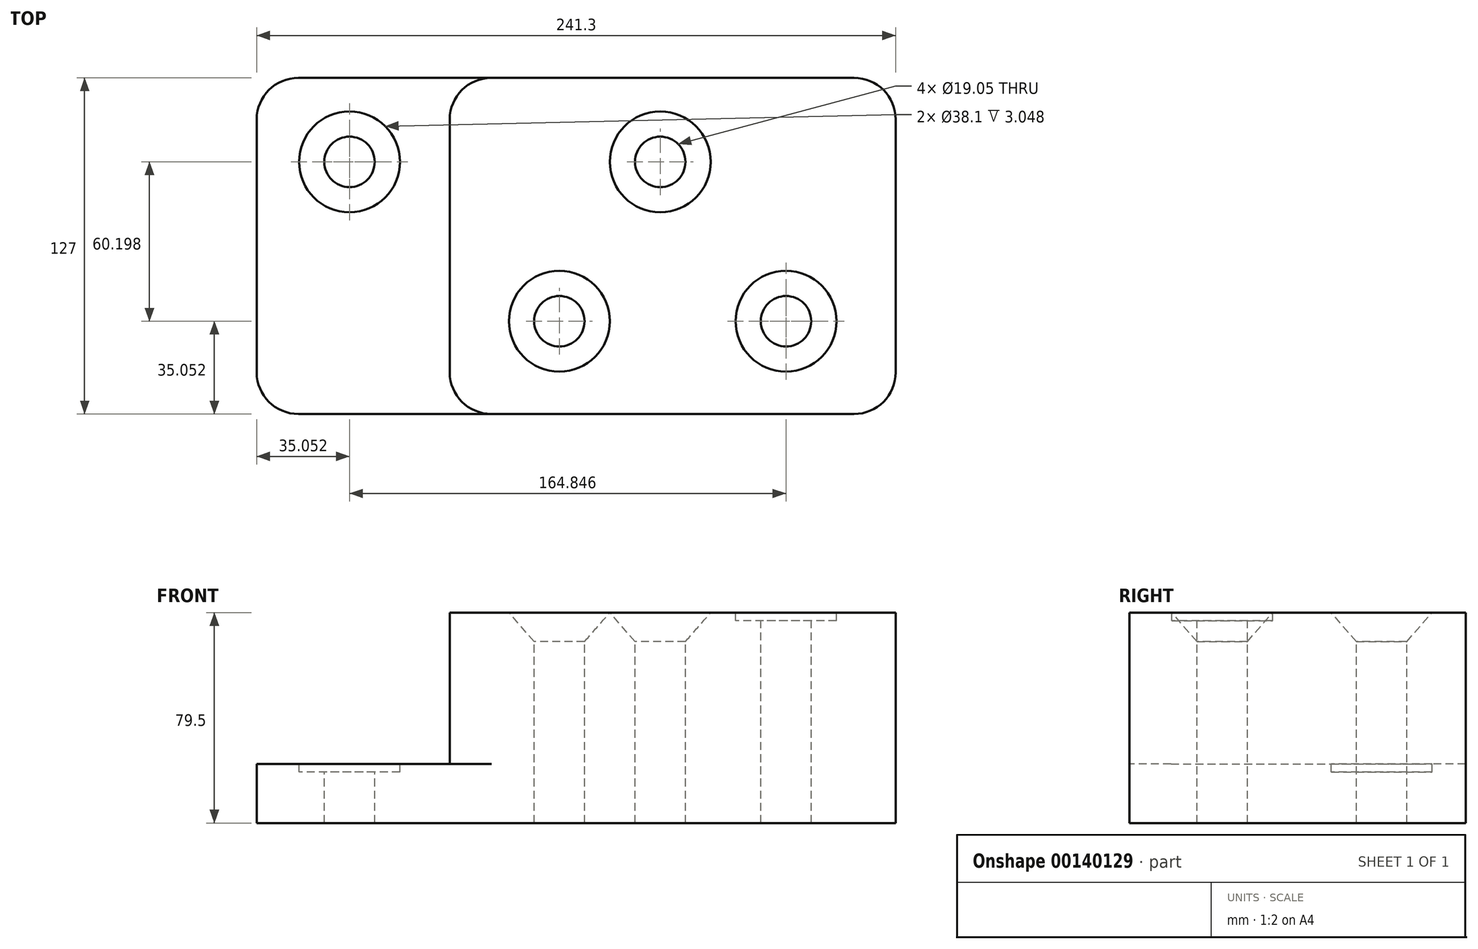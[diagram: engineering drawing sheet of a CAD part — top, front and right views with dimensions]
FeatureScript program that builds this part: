
annotation { "Feature Type Name" : "Feature", "Feature Type Description" : "" }
export const myFeature = defineFeature(function(context is Context, id is Id, definition is map)
    precondition{}
    {
        {
            var Q0;
            Q0=qCreatedBy(makeId("Top.planeOp"),FACE);
            var sketch = newSketch(context, id + "F0", { "sketchPlane" : qUnion([Q0])});
            skLineSegment(sketch, "E0.bottom", {"start": v(0, 0) * mm, "end": v(72.9, 0) * mm});
            skLineSegment(sketch, "E0.top", {"start": v(0, 127) * mm, "end": v(72.9, 127) * mm});
            skLineSegment(sketch, "E0.left", {"start": v(0, 0) * mm, "end": v(0, 127) * mm});
            skLineSegment(sketch, "E0.right", {"start": v(72.9, 0) * mm, "end": v(72.9, 127) * mm});
            skLineSegment(sketch, "E1.bottom", {"start": v(0, 0) * mm, "end": v(241.3, 0) * mm});
            skLineSegment(sketch, "E1.top", {"start": v(0, 127) * mm, "end": v(241.3, 127) * mm});
            skLineSegment(sketch, "E1.right", {"start": v(241.3, 0) * mm, "end": v(241.3, 127) * mm});
            skLineSegment(sketch, "E2", {"start": v(241.3, 127) * mm, "end": v(199.9, 127) * mm, "construction": true});
            skLineSegment(sketch, "E3", {"start": v(241.3, 127) * mm, "end": v(152.4, 127) * mm, "construction": true});
            skLineSegment(sketch, "E4", {"start": v(241.3, 127) * mm, "end": v(114.3, 127) * mm, "construction": true});
            skLineSegment(sketch, "E5", {"start": v(0, 127) * mm, "end": v(35.05, 127) * mm, "construction": true});
            skSolve(sketch);
        }
        {
            var Q0;
            {var subQ0=sQuery(id+"F0.wireOp",EDGE,"E0.right");Q0=makeQuery(id+"F0.imprint","IMPRINT",FACE,{"disambiguationData":[TD([[makeQuery(id+"F0.imprint","IMPRINT",EDGE,{"derivedFrom":subQ0}),1.0]])]});}
            extrude(context, id + "F1", {"entities" : qUnion([Q0]), "depth" : 22.35 * mm});
        }
        {
            var Q0;
            {var subQ0=sQuery(id+"F0.wireOp",EDGE,"E0.right");Q0=makeQuery(id+"F0.imprint","IMPRINT",FACE,{"disambiguationData":[TD([[makeQuery(id+"F0.imprint","IMPRINT",EDGE,{"derivedFrom":subQ0}),-1.0]])]});}
            extrude(context, id + "F2", {"entities" : qUnion([Q0]), "operationType" : NewBodyOperationType.ADD, "depth" : 79.5 * mm});
        }
        {
            var Q0;
            Q0=makeQuery(id+"F1.opExtrude","CAP_FACE",FACE,{"disambiguationData":[OSD([sQuery(id+"F0.wireOp",EDGE,"E0.right"),sQuery(id+"F0.wireOp",EDGE,"E1.bottom"),sQuery(id+"F0.wireOp",EDGE,"E1.top"),sQuery(id+"F0.wireOp",EDGE,"E0.left")])],"isStart":false});
            var sketch = newSketch(context, id + "F3", { "sketchPlane" : qUnion([Q0])});
            skLineSegment(sketch, "E6", {"start": v(0, 127) * mm, "end": v(35.05, 127) * mm, "construction": true});
            skLineSegment(sketch, "E7", {"start": v(35.05, 127) * mm, "end": v(35.05, 95.25) * mm, "construction": true});
            skPoint(sketch, "E8", {"position": v(35.05, 95.25) * mm});
            skSolve(sketch);
        }
        {
            var Q0;
            Q0=sQuery(id+"F3.wireOp",VERTEX,"E8");
            var Q1;
            Q1=makeQuery(id+"F1.opExtrude","SWEPT_BODY",BODY,{"disambiguationData":[OSD([sQuery(id+"F0.wireOp",EDGE,"E0.right"),sQuery(id+"F0.wireOp",EDGE,"E1.bottom"),sQuery(id+"F0.wireOp",EDGE,"E1.top"),sQuery(id+"F0.wireOp",EDGE,"E0.left")])]});
            hole(context, id + "F4", {"style" : HoleStyle.C_BORE, "endStyle" : HoleEndStyle.THROUGH, "holeDiameter" : 19.05 * mm, "cBoreDiameter" : 38.1 * mm, "cBoreDepth" : 3.05 * mm, "locations" : qUnion([Q0]), "scope" : qUnion([Q1]), "isTappedThrough" : true});
        }
        {
            var Q0;
            Q0=makeQuery(id+"F2.opExtrude","CAP_FACE",FACE,{"disambiguationData":[OSD([sQuery(id+"F0.wireOp",EDGE,"E0.right"),sQuery(id+"F0.wireOp",EDGE,"E1.bottom"),sQuery(id+"F0.wireOp",EDGE,"E1.top"),sQuery(id+"F0.wireOp",EDGE,"E1.right")])],"isStart":false});
            var sketch = newSketch(context, id + "F5", { "sketchPlane" : qUnion([Q0])});
            skLineSegment(sketch, "E9", {"start": v(241.3, 127) * mm, "end": v(199.9, 127) * mm, "construction": true});
            skLineSegment(sketch, "E10", {"start": v(199.9, 127) * mm, "end": v(199.9, 35.05) * mm, "construction": true});
            skLineSegment(sketch, "E11", {"start": v(241.3, 127) * mm, "end": v(152.4, 127) * mm, "construction": true});
            skLineSegment(sketch, "E12", {"start": v(152.4, 127) * mm, "end": v(152.4, 95.25) * mm, "construction": true});
            skLineSegment(sketch, "E13", {"start": v(241.3, 127) * mm, "end": v(114.3, 127) * mm, "construction": true});
            skLineSegment(sketch, "E14", {"start": v(114.3, 127) * mm, "end": v(114.3, 35.05) * mm, "construction": true});
            skPoint(sketch, "E15", {"position": v(114.3, 35.05) * mm});
            skPoint(sketch, "E16", {"position": v(152.4, 95.25) * mm});
            skPoint(sketch, "E17", {"position": v(199.9, 35.05) * mm});
            skSolve(sketch);
        }
        {
            var Q0;
            Q0=sQuery(id+"F5.wireOp",VERTEX,"E15");
            var Q1;
            Q1=sQuery(id+"F5.wireOp",VERTEX,"E16");
            var Q2;
            Q2=makeQuery(id+"F1.opExtrude","SWEPT_BODY",BODY,{"disambiguationData":[OSD([sQuery(id+"F0.wireOp",EDGE,"E0.right"),sQuery(id+"F0.wireOp",EDGE,"E1.bottom"),sQuery(id+"F0.wireOp",EDGE,"E1.top"),sQuery(id+"F0.wireOp",EDGE,"E0.left")])]});
            hole(context, id + "F6", {"style" : HoleStyle.C_SINK, "endStyle" : HoleEndStyle.THROUGH, "holeDiameter" : 19.05 * mm, "cSinkDiameter" : 38.1 * mm, "cSinkAngle" : 82 * degree, "locations" : qUnion([Q0, Q1]), "scope" : qUnion([Q2]), "isTappedThrough" : true});
        }
        {
            var Q0;
            Q0=sQuery(id+"F5.wireOp",VERTEX,"E17");
            var Q1;
            Q1=makeQuery(id+"F1.opExtrude","SWEPT_BODY",BODY,{"disambiguationData":[OSD([sQuery(id+"F0.wireOp",EDGE,"E0.right"),sQuery(id+"F0.wireOp",EDGE,"E1.bottom"),sQuery(id+"F0.wireOp",EDGE,"E1.top"),sQuery(id+"F0.wireOp",EDGE,"E0.left")])]});
            hole(context, id + "F7", {"style" : HoleStyle.C_BORE, "endStyle" : HoleEndStyle.THROUGH, "holeDiameter" : 19.05 * mm, "cBoreDiameter" : 38.1 * mm, "cBoreDepth" : 3.05 * mm, "locations" : qUnion([Q0]), "scope" : qUnion([Q1]), "isTappedThrough" : true});
        }
        {
            var Q0;
            Q0=makeQuery(id+"F1.opExtrude","SWEPT_EDGE",EDGE,{"disambiguationData":[OSD([sQuery(id+"F0.wireOp",EDGE,"E1.bottom"),sQuery(id+"F0.wireOp",EDGE,"E0.left")])]});
            var Q1;
            Q1=makeQuery(id+"F1.opExtrude","SWEPT_EDGE",EDGE,{"disambiguationData":[OSD([sQuery(id+"F0.wireOp",EDGE,"E1.top"),sQuery(id+"F0.wireOp",EDGE,"E0.left")])]});
            var Q2;
            Q2=makeQuery(id+"F2.opExtrude","SWEPT_EDGE",EDGE,{"disambiguationData":[OSD([sQuery(id+"F0.wireOp",EDGE,"E0.right"),sQuery(id+"F0.wireOp",EDGE,"E1.top")])]});
            var Q3;
            Q3=makeQuery(id+"F2.opExtrude","SWEPT_EDGE",EDGE,{"disambiguationData":[OSD([sQuery(id+"F0.wireOp",EDGE,"E0.right"),sQuery(id+"F0.wireOp",EDGE,"E1.bottom")])]});
            var Q4;
            Q4=makeQuery(id+"F2.opExtrude","SWEPT_EDGE",EDGE,{"disambiguationData":[OSD([sQuery(id+"F0.wireOp",EDGE,"E1.bottom"),sQuery(id+"F0.wireOp",EDGE,"E1.right")])]});
            var Q5;
            Q5=makeQuery(id+"F2.opExtrude","SWEPT_EDGE",EDGE,{"disambiguationData":[OSD([sQuery(id+"F0.wireOp",EDGE,"E1.top"),sQuery(id+"F0.wireOp",EDGE,"E1.right")])]});
            fillet(context, id + "F8", {"entities" : qUnion([Q0, Q1, Q2, Q3, Q4, Q5]), "radius" : 15.75 * mm, "tangentPropagation" : true, "allowEdgeOverflow" : false});
        }
    });
